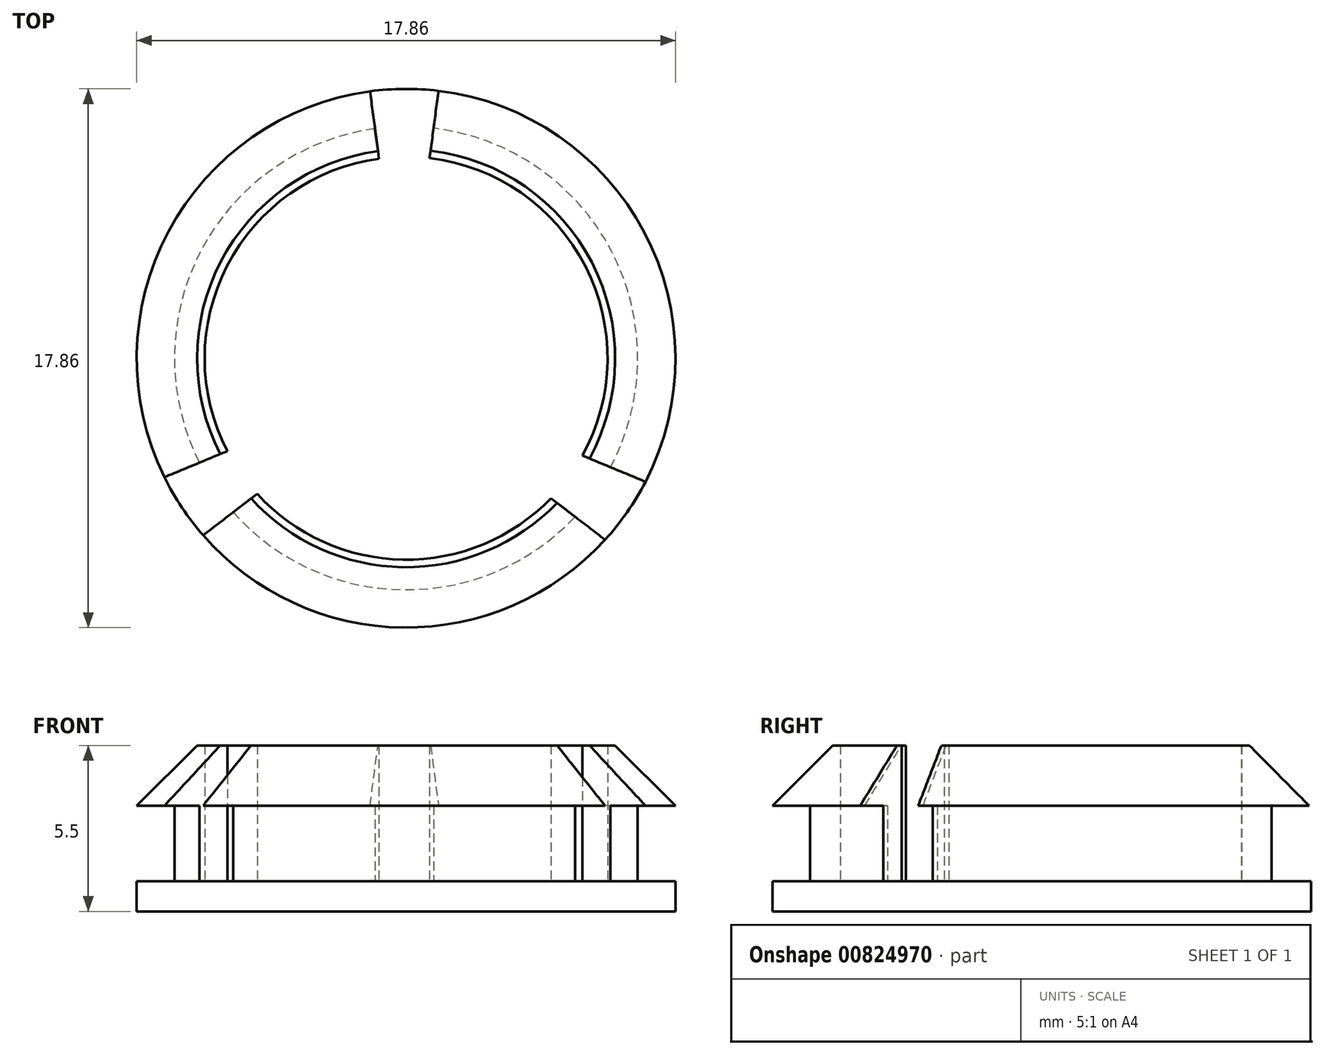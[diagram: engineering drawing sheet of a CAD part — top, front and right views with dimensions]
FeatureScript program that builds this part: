
annotation { "Feature Type Name" : "Feature", "Feature Type Description" : "" }
export const myFeature = defineFeature(function(context is Context, id is Id, definition is map)
    precondition{}
    {
        {
            var Q0;
            Q0=qCreatedBy(makeId("Top.planeOp"),FACE);
            var sketch = newSketch(context, id + "F0", { "sketchPlane" : qUnion([Q0])});
            skCircle(sketch, "E0", {"center": v(0, 0) * mm, "radius": 8.93 * mm});
            skCircle(sketch, "E1", {"center": v(0, 0) * mm, "radius": 7.68 * mm});
            skCircle(sketch, "E2", {"center": v(0, 0) * mm, "radius": 6.68 * mm});
            skLineSegment(sketch, "E3", {"start": v(-1.2, 8.84) * mm, "end": v(-0.9, 6.61) * mm});
            skLineSegment(sketch, "E4", {"start": v(0.78, 6.63) * mm, "end": v(1.07, 8.86) * mm});
            skLineSegment(sketch, "E5", {"start": v(5.84, -3.23) * mm, "end": v(7.93, -4.1) * mm});
            skLineSegment(sketch, "E6", {"start": v(4.8, -4.64) * mm, "end": v(6.6, -6.02) * mm});
            skLineSegment(sketch, "E7", {"start": v(-6.73, -5.87) * mm, "end": v(-4.94, -4.5) * mm});
            skLineSegment(sketch, "E8", {"start": v(-8, -3.94) * mm, "end": v(-5.92, -3.08) * mm});
            skLineSegment(sketch, "E9", {"start": v(0, -6.68) * mm, "end": v(0, -8.93) * mm});
            skSolve(sketch);
        }
        {
            var Q0;
            {var subQ0=sQuery(id+"F0.wireOp",EDGE,"E2");var subQ4=makeQuery(id+"F0.imprint","INTERSECT",VERTEX,{"derivedFrom":[subQ0,sQuery(id+"F0.wireOp",EDGE,"E3")]});Q0=makeQuery(id+"F0.imprint","IMPRINT",FACE,{"disambiguationData":[TD([[makeQuery(id+"F0.imprint","IMPRINT",EDGE,{"disambiguationData":[TD([[subQ4,1.0]])],"derivedFrom":subQ0}),1.0]])]});}
            var Q1;
            {var subQ0=sQuery(id+"F0.wireOp",EDGE,"E8");var subQ1=sQuery(id+"F0.wireOp",EDGE,"E1");var subQ2=makeQuery(id+"F0.imprint","INTERSECT",VERTEX,{"derivedFrom":[subQ1,subQ0]});Q1=makeQuery(id+"F0.imprint","IMPRINT",FACE,{"disambiguationData":[TD([[makeQuery(id+"F0.imprint","IMPRINT",EDGE,{"disambiguationData":[TD([[subQ2,-1.0]])],"derivedFrom":subQ1}),1.0]])]});}
            var Q2;
            {var subQ0=sQuery(id+"F0.wireOp",EDGE,"E7");var subQ1=sQuery(id+"F0.wireOp",EDGE,"E0");var subQ2=makeQuery(id+"F0.imprint","INTERSECT",VERTEX,{"derivedFrom":[subQ1,subQ0]});Q2=makeQuery(id+"F0.imprint","IMPRINT",FACE,{"disambiguationData":[TD([[makeQuery(id+"F0.imprint","IMPRINT",EDGE,{"disambiguationData":[TD([[subQ2,1.0]])],"derivedFrom":subQ1}),1.0]])]});}
            var Q3;
            Q3=makeQuery(id+"F0.imprint","IMPRINT",FACE,{"disambiguationData":[TD([[makeQuery(id+"F0.imprint","IMPRINT",EDGE,{"derivedFrom":sQuery(id+"F0.wireOp",EDGE,"E0")}),1.0]])]});
            var Q4;
            {var subQ0=sQuery(id+"F0.wireOp",EDGE,"E6");var subQ1=sQuery(id+"F0.wireOp",EDGE,"E1");var subQ2=makeQuery(id+"F0.imprint","INTERSECT",VERTEX,{"derivedFrom":[subQ1,subQ0]});Q4=makeQuery(id+"F0.imprint","IMPRINT",FACE,{"disambiguationData":[TD([[makeQuery(id+"F0.imprint","IMPRINT",EDGE,{"disambiguationData":[TD([[subQ2,-1.0]])],"derivedFrom":subQ1}),1.0]])]});}
            var Q5;
            {var subQ0=sQuery(id+"F0.wireOp",EDGE,"E5");var subQ1=sQuery(id+"F0.wireOp",EDGE,"E0");var subQ2=makeQuery(id+"F0.imprint","INTERSECT",VERTEX,{"derivedFrom":[subQ1,subQ0]});Q5=makeQuery(id+"F0.imprint","IMPRINT",FACE,{"disambiguationData":[TD([[makeQuery(id+"F0.imprint","IMPRINT",EDGE,{"disambiguationData":[TD([[subQ2,1.0]])],"derivedFrom":subQ1}),1.0]])]});}
            var Q6;
            {var subQ0=sQuery(id+"F0.wireOp",EDGE,"E3");var subQ1=sQuery(id+"F0.wireOp",EDGE,"E1");var subQ2=makeQuery(id+"F0.imprint","INTERSECT",VERTEX,{"derivedFrom":[subQ1,subQ0]});Q6=makeQuery(id+"F0.imprint","IMPRINT",FACE,{"disambiguationData":[TD([[makeQuery(id+"F0.imprint","IMPRINT",EDGE,{"disambiguationData":[TD([[subQ2,1.0]])],"derivedFrom":subQ1}),1.0]])]});}
            var Q7;
            {var subQ0=sQuery(id+"F0.wireOp",EDGE,"E3");var subQ1=sQuery(id+"F0.wireOp",EDGE,"E0");var subQ2=makeQuery(id+"F0.imprint","INTERSECT",VERTEX,{"derivedFrom":[subQ1,subQ0]});Q7=makeQuery(id+"F0.imprint","IMPRINT",FACE,{"disambiguationData":[TD([[makeQuery(id+"F0.imprint","IMPRINT",EDGE,{"disambiguationData":[TD([[subQ2,1.0]])],"derivedFrom":subQ1}),1.0]])]});}
            var Q8;
            {var subQ0=sQuery(id+"F0.wireOp",EDGE,"E7");var subQ1=sQuery(id+"F0.wireOp",EDGE,"E0");var subQ2=makeQuery(id+"F0.imprint","INTERSECT",VERTEX,{"derivedFrom":[subQ1,subQ0]});Q8=makeQuery(id+"F0.imprint","IMPRINT",FACE,{"disambiguationData":[TD([[makeQuery(id+"F0.imprint","IMPRINT",EDGE,{"disambiguationData":[TD([[subQ2,-1.0]])],"derivedFrom":subQ1}),1.0]])]});}
            var Q9;
            {var subQ0=sQuery(id+"F0.wireOp",EDGE,"E6");var subQ1=sQuery(id+"F0.wireOp",EDGE,"E0");var subQ2=makeQuery(id+"F0.imprint","INTERSECT",VERTEX,{"derivedFrom":[subQ1,subQ0]});Q9=makeQuery(id+"F0.imprint","IMPRINT",FACE,{"disambiguationData":[TD([[makeQuery(id+"F0.imprint","IMPRINT",EDGE,{"disambiguationData":[TD([[subQ2,1.0]])],"derivedFrom":subQ1}),1.0]])]});}
            var Q10;
            {var subQ0=sQuery(id+"F0.wireOp",EDGE,"E4");var subQ1=sQuery(id+"F0.wireOp",EDGE,"E0");var subQ2=makeQuery(id+"F0.imprint","INTERSECT",VERTEX,{"derivedFrom":[subQ1,subQ0]});Q10=makeQuery(id+"F0.imprint","IMPRINT",FACE,{"disambiguationData":[TD([[makeQuery(id+"F0.imprint","IMPRINT",EDGE,{"disambiguationData":[TD([[subQ2,1.0]])],"derivedFrom":subQ1}),1.0]])]});}
            var Q11;
            {var subQ0=sQuery(id+"F0.wireOp",EDGE,"E3");var subQ1=sQuery(id+"F0.wireOp",EDGE,"E0");var subQ2=makeQuery(id+"F0.imprint","INTERSECT",VERTEX,{"derivedFrom":[subQ1,subQ0]});Q11=makeQuery(id+"F0.imprint","IMPRINT",FACE,{"disambiguationData":[TD([[makeQuery(id+"F0.imprint","IMPRINT",EDGE,{"disambiguationData":[TD([[subQ2,-1.0]])],"derivedFrom":subQ1}),1.0]])]});}
            extrude(context, id + "F1", {"entities" : qUnion([Q0, Q1, Q2, Q3, Q4, Q5, Q6, Q7, Q8, Q9, Q10, Q11]), "depth" : 1 * mm, "offsetDistance" : 25 * mm});
        }
        {
            var Q0;
            {var subQ0=sQuery(id+"F0.wireOp",EDGE,"E3");var subQ1=sQuery(id+"F0.wireOp",EDGE,"E1");var subQ2=makeQuery(id+"F0.imprint","INTERSECT",VERTEX,{"derivedFrom":[subQ1,subQ0]});Q0=makeQuery(id+"F0.imprint","IMPRINT",FACE,{"disambiguationData":[TD([[makeQuery(id+"F0.imprint","IMPRINT",EDGE,{"disambiguationData":[TD([[subQ2,-1.0]])],"derivedFrom":subQ1}),1.0]])]});}
            var Q1;
            {var subQ0=sQuery(id+"F0.wireOp",EDGE,"E4");var subQ1=sQuery(id+"F0.wireOp",EDGE,"E1");var subQ2=makeQuery(id+"F0.imprint","INTERSECT",VERTEX,{"derivedFrom":[subQ1,subQ0]});Q1=makeQuery(id+"F0.imprint","IMPRINT",FACE,{"disambiguationData":[TD([[makeQuery(id+"F0.imprint","IMPRINT",EDGE,{"disambiguationData":[TD([[subQ2,1.0]])],"derivedFrom":subQ1}),1.0]])]});}
            var Q2;
            {var subQ0=sQuery(id+"F0.wireOp",EDGE,"E7");var subQ1=sQuery(id+"F0.wireOp",EDGE,"E1");var subQ2=makeQuery(id+"F0.imprint","INTERSECT",VERTEX,{"derivedFrom":[subQ1,subQ0]});Q2=makeQuery(id+"F0.imprint","IMPRINT",FACE,{"disambiguationData":[TD([[makeQuery(id+"F0.imprint","IMPRINT",EDGE,{"disambiguationData":[TD([[subQ2,-1.0]])],"derivedFrom":subQ1}),1.0]])]});}
            var Q3;
            {var subQ0=sQuery(id+"F0.wireOp",EDGE,"E9");var subQ1=sQuery(id+"F0.wireOp",EDGE,"E1");var subQ2=makeQuery(id+"F0.imprint","INTERSECT",VERTEX,{"derivedFrom":[subQ1,subQ0]});Q3=makeQuery(id+"F0.imprint","IMPRINT",FACE,{"disambiguationData":[TD([[makeQuery(id+"F0.imprint","IMPRINT",EDGE,{"disambiguationData":[TD([[subQ2,-1.0]])],"derivedFrom":subQ1}),1.0]])]});}
            extrude(context, id + "F2", {"entities" : qUnion([Q0, Q1, Q2, Q3]), "operationType" : NewBodyOperationType.ADD, "depth" : 5.5 * mm, "offsetDistance" : 25 * mm});
        }
        {
            var Q0;
            {var subQ0=sQuery(id+"F0.wireOp",EDGE,"E3");var subQ1=sQuery(id+"F0.wireOp",EDGE,"E0");var subQ2=makeQuery(id+"F0.imprint","INTERSECT",VERTEX,{"derivedFrom":[subQ1,subQ0]});Q0=makeQuery(id+"F0.imprint","IMPRINT",FACE,{"disambiguationData":[TD([[makeQuery(id+"F0.imprint","IMPRINT",EDGE,{"disambiguationData":[TD([[subQ2,-1.0]])],"derivedFrom":subQ1}),1.0]])]});}
            var Q1;
            {var subQ0=sQuery(id+"F0.wireOp",EDGE,"E4");var subQ1=sQuery(id+"F0.wireOp",EDGE,"E0");var subQ2=makeQuery(id+"F0.imprint","INTERSECT",VERTEX,{"derivedFrom":[subQ1,subQ0]});Q1=makeQuery(id+"F0.imprint","IMPRINT",FACE,{"disambiguationData":[TD([[makeQuery(id+"F0.imprint","IMPRINT",EDGE,{"disambiguationData":[TD([[subQ2,1.0]])],"derivedFrom":subQ1}),1.0]])]});}
            var Q2;
            {var subQ0=sQuery(id+"F0.wireOp",EDGE,"E6");var subQ1=sQuery(id+"F0.wireOp",EDGE,"E0");var subQ2=makeQuery(id+"F0.imprint","INTERSECT",VERTEX,{"derivedFrom":[subQ1,subQ0]});Q2=makeQuery(id+"F0.imprint","IMPRINT",FACE,{"disambiguationData":[TD([[makeQuery(id+"F0.imprint","IMPRINT",EDGE,{"disambiguationData":[TD([[subQ2,1.0]])],"derivedFrom":subQ1}),1.0]])]});}
            var Q3;
            {var subQ0=sQuery(id+"F0.wireOp",EDGE,"E7");var subQ1=sQuery(id+"F0.wireOp",EDGE,"E0");var subQ2=makeQuery(id+"F0.imprint","INTERSECT",VERTEX,{"derivedFrom":[subQ1,subQ0]});Q3=makeQuery(id+"F0.imprint","IMPRINT",FACE,{"disambiguationData":[TD([[makeQuery(id+"F0.imprint","IMPRINT",EDGE,{"disambiguationData":[TD([[subQ2,-1.0]])],"derivedFrom":subQ1}),1.0]])]});}
            extrude(context, id + "F3", {"entities" : qUnion([Q0, Q1, Q2, Q3]), "operationType" : NewBodyOperationType.ADD, "depth" : 5.5 * mm, "offsetDistance" : 25 * mm, "hasSecondDirection" : true, "secondDirectionOppositeDirection" : false, "secondDirectionDepth" : 3.5 * mm});
        }
        {
            var Q0;
            {var subQ0=sQuery(id+"F0.wireOp",EDGE,"E0");Q0=makeQuery(id+"F3.opExtrude","CAP_EDGE",EDGE,{"disambiguationData":[OSD([subQ0]),TDD([makeQuery(id+"F0.imprint","IMPRINT",EDGE,{"disambiguationData":[TD([[makeQuery(id+"F0.imprint","INTERSECT",VERTEX,{"derivedFrom":[subQ0,sQuery(id+"F0.wireOp",EDGE,"E3")]}),-1.0]])],"derivedFrom":subQ0})])],"isStart":false});}
            var Q1;
            {var subQ0=sQuery(id+"F0.wireOp",EDGE,"E0");Q1=makeQuery(id+"F3.opExtrude","CAP_EDGE",EDGE,{"disambiguationData":[OSD([subQ0]),TDD([makeQuery(id+"F0.imprint","IMPRINT",EDGE,{"disambiguationData":[TD([[makeQuery(id+"F0.imprint","INTERSECT",VERTEX,{"derivedFrom":[subQ0,sQuery(id+"F0.wireOp",EDGE,"E7")]}),-1.0]])],"derivedFrom":subQ0}),makeQuery(id+"F0.imprint","IMPRINT",EDGE,{"disambiguationData":[TD([[makeQuery(id+"F0.imprint","INTERSECT",VERTEX,{"derivedFrom":[subQ0,sQuery(id+"F0.wireOp",EDGE,"E6")]}),1.0]])],"derivedFrom":subQ0})])],"isStart":false});}
            var Q2;
            {var subQ0=sQuery(id+"F0.wireOp",EDGE,"E0");Q2=makeQuery(id+"F3.opExtrude","CAP_EDGE",EDGE,{"disambiguationData":[OSD([subQ0]),TDD([makeQuery(id+"F0.imprint","IMPRINT",EDGE,{"disambiguationData":[TD([[makeQuery(id+"F0.imprint","INTERSECT",VERTEX,{"derivedFrom":[subQ0,sQuery(id+"F0.wireOp",EDGE,"E4")]}),1.0]])],"derivedFrom":subQ0})])],"isStart":false});}
            chamfer(context, id + "F4", {"entities" : qUnion([Q0, Q1, Q2]), "width" : 2 * mm, "tangentPropagation" : true});
        }
    });
